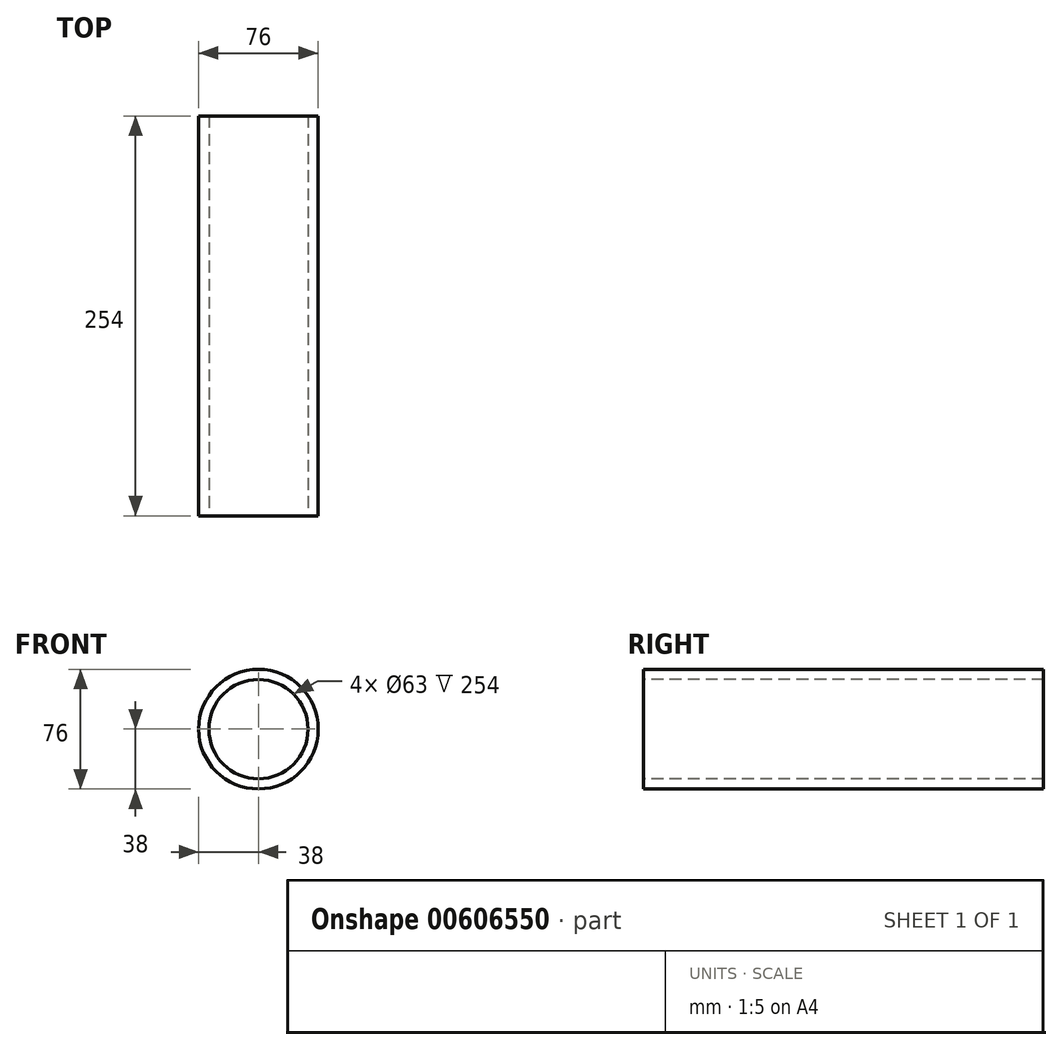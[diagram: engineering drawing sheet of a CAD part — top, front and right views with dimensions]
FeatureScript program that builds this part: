
annotation { "Feature Type Name" : "Feature", "Feature Type Description" : "" }
export const myFeature = defineFeature(function(context is Context, id is Id, definition is map)
    precondition{}
    {
        {
            var Q0;
            Q0=qCreatedBy(makeId("Front.planeOp"),FACE);
            var sketch = newSketch(context, id + "F0", { "sketchPlane" : qUnion([Q0])});
            skCircle(sketch, "E0", {"center": v(0, 0) * mm, "radius": 38 * mm});
            skCircle(sketch, "E1", {"center": v(0, 0) * mm, "radius": 31.5 * mm});
            skSolve(sketch);
        }
        {
            var Q0;
            Q0=makeQuery(id+"F0.imprint","IMPRINT",FACE,{"disambiguationData":[TD([[makeQuery(id+"F0.imprint","IMPRINT",EDGE,{"derivedFrom":sQuery(id+"F0.wireOp",EDGE,"E0")}),1.0]])]});
            extrude(context, id + "F1", {"entities" : qUnion([Q0]), "oppositeDirection" : true, "depth" : 254 * mm, "offsetDistance" : 25 * mm});
        }
    });
